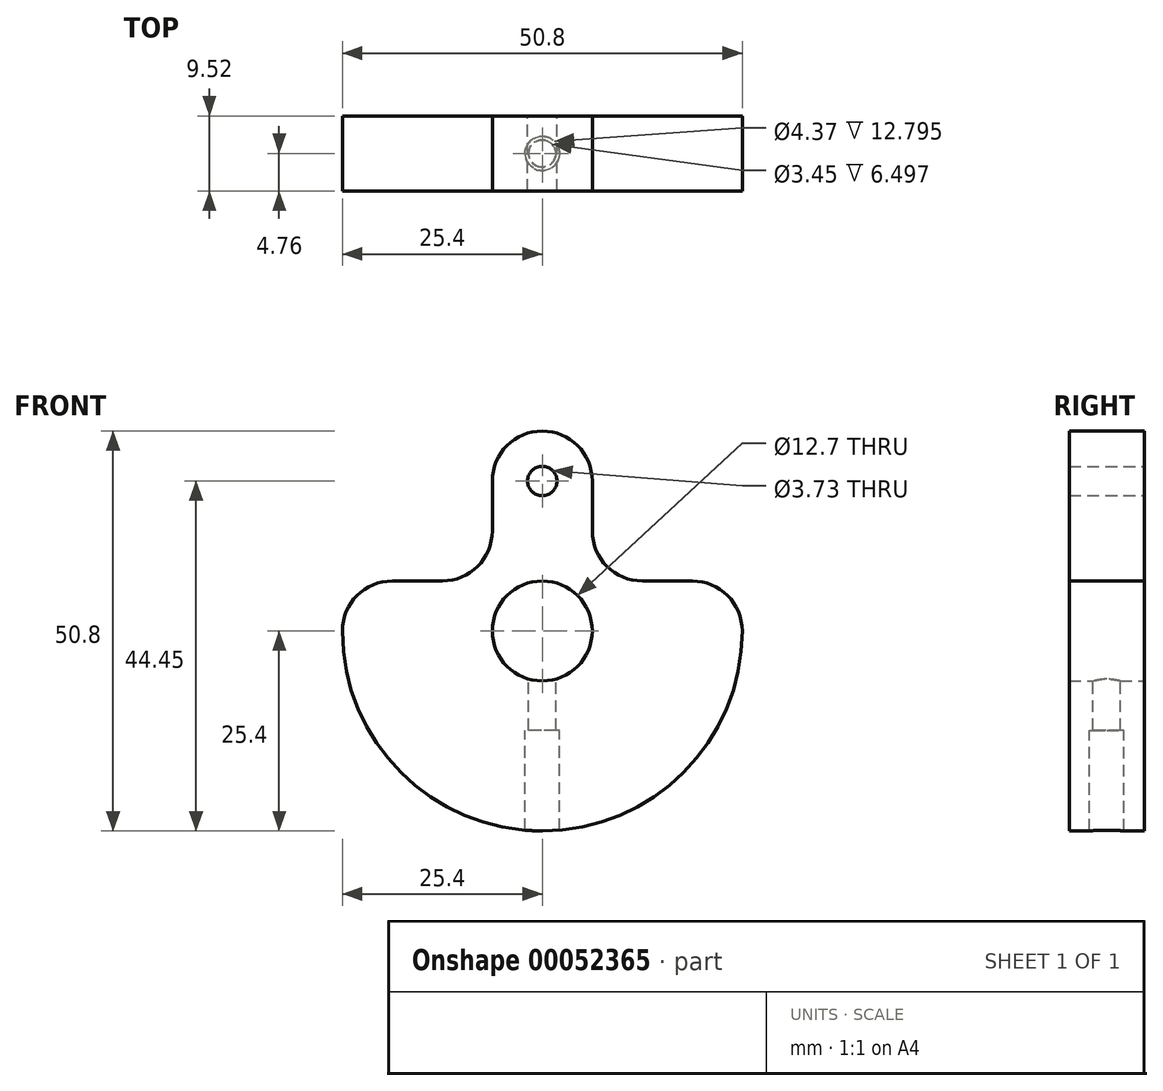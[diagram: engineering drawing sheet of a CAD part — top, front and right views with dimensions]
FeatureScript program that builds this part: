
annotation { "Feature Type Name" : "Feature", "Feature Type Description" : "" }
export const myFeature = defineFeature(function(context is Context, id is Id, definition is map)
    precondition{}
    {
        {
            var Q0;
            Q0=qCreatedBy(makeId("Front.planeOp"),FACE);
            var sketch = newSketch(context, id + "F0", { "sketchPlane" : qUnion([Q0])});
            skArc(sketch, "E0", {"start": v(25.4, 0) * mm, "mid": v(0, -25.4) * mm, "end": v(-25.4, 0) * mm});
            skCircle(sketch, "E1", {"center": v(0, 0) * mm, "radius": 6.35 * mm});
            skCircle(sketch, "E2", {"center": v(0, 19.05) * mm, "radius": 1.87 * mm});
            skArc(sketch, "E3", {"start": v(-6.35, 19.05) * mm, "mid": v(0, 25.4) * mm, "end": v(6.35, 19.05) * mm});
            skLineSegment(sketch, "E4", {"start": v(-6.35, 19.05) * mm, "end": v(-6.35, 12.7) * mm});
            skLineSegment(sketch, "E5", {"start": v(6.35, 19.05) * mm, "end": v(6.35, 12.7) * mm});
            skLineSegment(sketch, "E6", {"start": v(-12.7, 6.35) * mm, "end": v(-19.05, 6.35) * mm});
            skLineSegment(sketch, "E7", {"start": v(12.7, 6.35) * mm, "end": v(19.05, 6.35) * mm});
            skArc(sketch, "E8", {"start": v(25.4, 0) * mm, "mid": v(23.54, 4.5) * mm, "end": v(19.05, 6.35) * mm});
            skArc(sketch, "E9", {"start": v(-25.4, 0) * mm, "mid": v(-23.54, 4.5) * mm, "end": v(-19.05, 6.35) * mm});
            skArc(sketch, "E10", {"start": v(-6.35, 12.7) * mm, "mid": v(-8.2, 8.2) * mm, "end": v(-12.7, 6.35) * mm});
            skArc(sketch, "E11", {"start": v(6.35, 12.7) * mm, "mid": v(8.2, 8.2) * mm, "end": v(12.7, 6.35) * mm});
            skPoint(sketch, "E12.orphan", {"position": v(-6.35, 6.35) * mm});
            skPoint(sketch, "E13.orphan", {"position": v(6.35, 6.35) * mm});
            skSolve(sketch);
        }
        {
            var Q0;
            Q0 = qSketchRegion(id + "F0", true);
            extrude(context, id + "F1", {"entities" : qUnion([Q0]), "depth" : 9.52 * mm, "symmetric" : true});
        }
        {
            var Q0;
            Q0=qCreatedBy(makeId("Top.planeOp"),FACE);
            cPlane(context, id + "F2", {"entities" : qUnion([Q0]), "cplaneType" : CPlaneType.OFFSET, "offset" : 25.4 * mm, "oppositeDirection" : true, "width" : 152.4 * mm, "height" : 152.4 * mm});
        }
        {
            var Q0;
            Q0=qCreatedBy(id+"F2.planeOp",FACE);
            var sketch = newSketch(context, id + "F3", { "sketchPlane" : qUnion([Q0])});
            skPoint(sketch, "E14", {"position": v(0, 0) * mm});
            skSolve(sketch);
        }
        {
            var Q0;
            Q0=sQuery(id+"F3.wireOp",VERTEX,"E14");
            var Q1;
            Q1=makeQuery(id+"F1.opExtrude","SWEPT_BODY",BODY,{"disambiguationData":[OSD([sQuery(id+"F0.wireOp",EDGE,"E0"),sQuery(id+"F0.wireOp",EDGE,"E1"),sQuery(id+"F0.wireOp",EDGE,"E2"),sQuery(id+"F0.wireOp",EDGE,"E3"),sQuery(id+"F0.wireOp",EDGE,"E4"),sQuery(id+"F0.wireOp",EDGE,"E5"),sQuery(id+"F0.wireOp",EDGE,"E6"),sQuery(id+"F0.wireOp",EDGE,"E7"),sQuery(id+"F0.wireOp",EDGE,"E8"),sQuery(id+"F0.wireOp",EDGE,"E9"),sQuery(id+"F0.wireOp",EDGE,"E10"),sQuery(id+"F0.wireOp",EDGE,"E11")])]});
            hole(context, id + "F4", {"style" : HoleStyle.C_BORE, "holeDiameter" : 3.45 * mm, "cBoreDiameter" : 4.37 * mm, "cBoreDepth" : 12.7 * mm, "endStyle" : HoleEndStyle.BLIND, "oppositeDirection" : true, "holeDepth" : 25.4 * mm, "locations" : qUnion([Q0]), "scope" : qUnion([Q1])});
        }
    });
